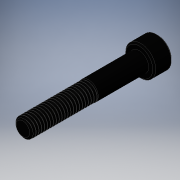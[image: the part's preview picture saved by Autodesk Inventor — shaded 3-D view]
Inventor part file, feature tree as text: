
AUTODESK INVENTOR PART (.ipt)
format: ipt  version: 2016 (Build 200138000, 138)  size: 738,304 bytes
history: native  units: in
note: dims shown in document units (in); Inventor stores cm internally (conversion verified against a paired STEP export)
features: chamfer x1
ambient origin geometry x8: Origin, YZ Plane, XZ Plane, XY Plane, X Axis, Y Axis, Z Axis, Center Point
bodies: Solid1 (feature_tree)
feature tree (1):
  chamfer  "Chamfer1"  [1 undecoded]
note: 1 required parameter value undecoded (feature->parameter linkage not recoverable at this tier; creation-order binding heuristic only, values carry confidence <= 0.55)
